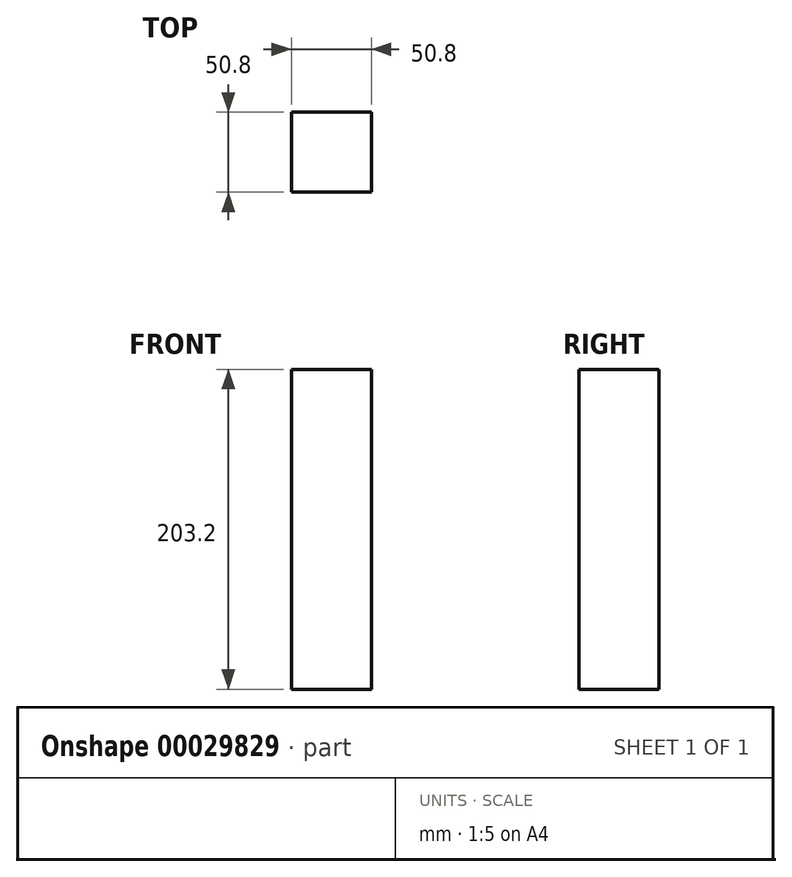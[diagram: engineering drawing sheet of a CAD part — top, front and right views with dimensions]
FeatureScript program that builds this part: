
annotation { "Feature Type Name" : "Feature", "Feature Type Description" : "" }
export const myFeature = defineFeature(function(context is Context, id is Id, definition is map)
    precondition{}
    {
        {
            var Q0;
            Q0=qCreatedBy(makeId("Top.planeOp"),FACE);
            var sketch = newSketch(context, id + "F0", { "sketchPlane" : qUnion([Q0])});
            skLineSegment(sketch, "E0.rect.bottom", {"start": v(-25.4, 25.4) * mm, "end": v(25.4, 25.4) * mm});
            skLineSegment(sketch, "E0.rect.top", {"start": v(-25.4, -25.4) * mm, "end": v(25.4, -25.4) * mm});
            skLineSegment(sketch, "E0.rect.left", {"start": v(-25.4, 25.4) * mm, "end": v(-25.4, -25.4) * mm});
            skLineSegment(sketch, "E0.rect.right", {"start": v(25.4, 25.4) * mm, "end": v(25.4, -25.4) * mm});
            skPoint(sketch, "E0.rect.middle", {"position": v(0, 0) * mm});
            skSolve(sketch);
        }
        {
            var Q0;
            Q0=makeQuery(id+"F0.imprint","IMPRINT",FACE,{"disambiguationData":[TD([[makeQuery(id+"F0.imprint","IMPRINT",EDGE,{"derivedFrom":sQuery(id+"F0.wireOp",EDGE,"E0.rect.bottom")}),-1.0]])]});
            extrude(context, id + "F1", {"entities" : qUnion([Q0]), "depth" : 203.2 * mm});
        }
    });
